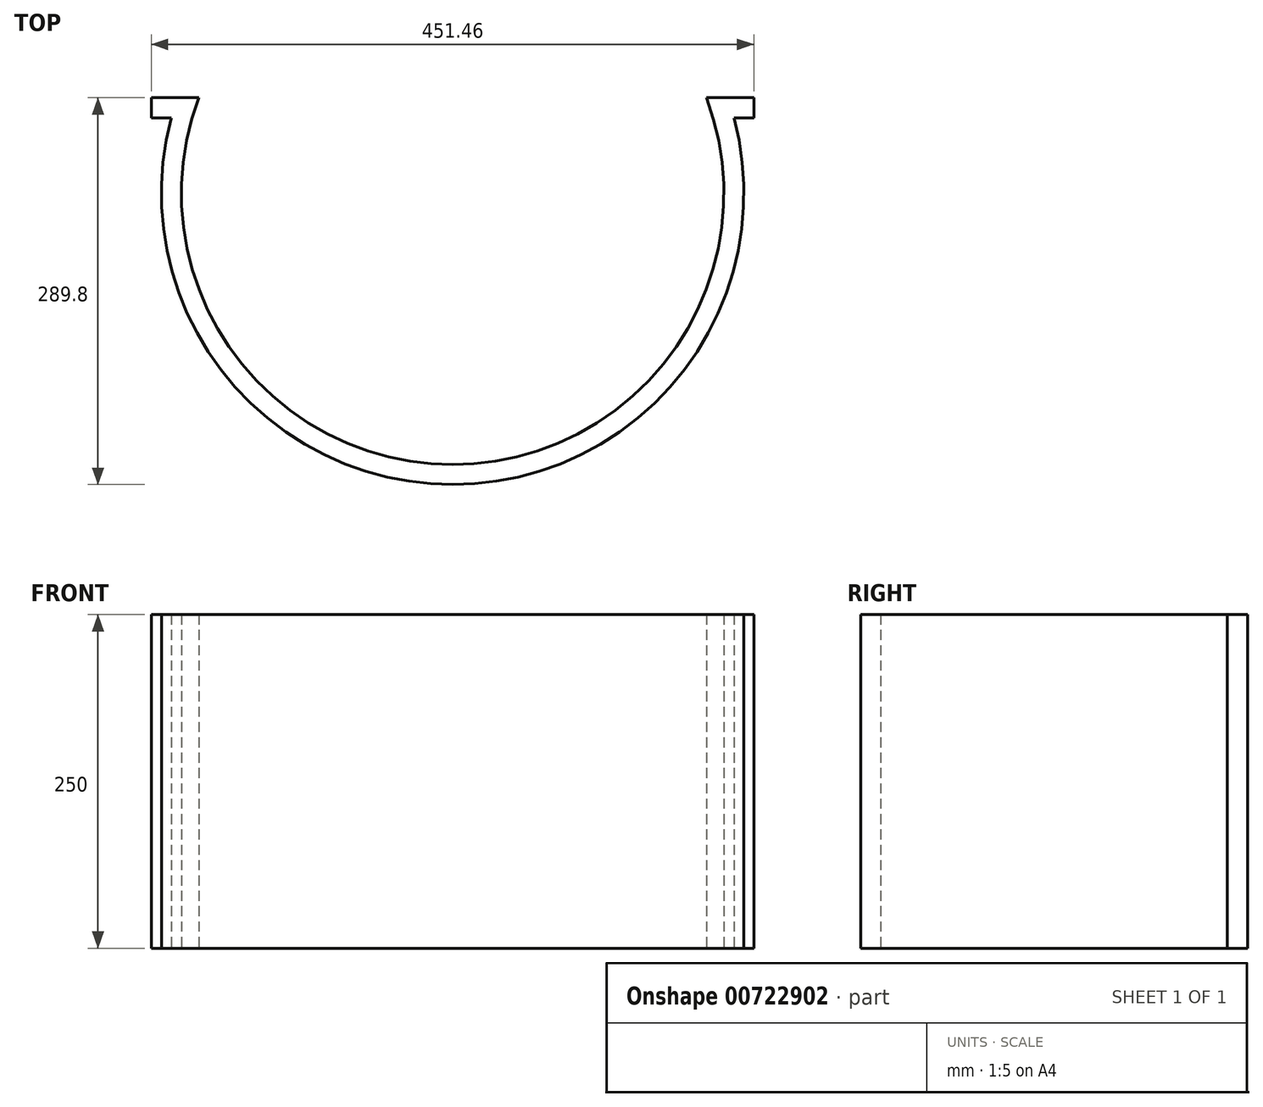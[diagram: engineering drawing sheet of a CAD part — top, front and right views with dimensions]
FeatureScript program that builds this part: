
annotation { "Feature Type Name" : "Feature", "Feature Type Description" : "" }
export const myFeature = defineFeature(function(context is Context, id is Id, definition is map)
    precondition{}
    {
        {
            var Q0;
            Q0=qCreatedBy(makeId("Top.planeOp"),FACE);
            var sketch = newSketch(context, id + "F0", { "sketchPlane" : qUnion([Q0])});
            skCircle(sketch, "E0", {"center": v(0, 0) * mm, "radius": 218.2 * mm});
            skCircle(sketch, "E1.0", {"center": v(0, 0) * mm, "radius": 203.2 * mm});
            skLineSegment(sketch, "E2", {"start": v(-206.12, 71.6) * mm, "end": v(206.12, 71.6) * mm});
            skLineSegment(sketch, "E3", {"start": v(206.12, 71.6) * mm, "end": v(225.73, 71.6) * mm});
            skLineSegment(sketch, "E4", {"start": v(225.73, 71.6) * mm, "end": v(225.73, 56.6) * mm});
            skLineSegment(sketch, "E5", {"start": v(225.73, 56.6) * mm, "end": v(210.73, 56.6) * mm});
            skLineSegment(sketch, "E6", {"start": v(-206.12, 71.6) * mm, "end": v(-225.73, 71.6) * mm});
            skLineSegment(sketch, "E7", {"start": v(-225.73, 71.6) * mm, "end": v(-225.73, 56.6) * mm});
            skLineSegment(sketch, "E8", {"start": v(-225.73, 56.6) * mm, "end": v(-210.73, 56.6) * mm});
            skSolve(sketch);
        }
        {
            var Q0;
            Q0=makeQuery(id+"F0.imprint","IMPRINT",FACE,{"disambiguationData":[TD([[makeQuery(id+"F0.imprint","IMPRINT",EDGE,{"derivedFrom":sQuery(id+"F0.wireOp",EDGE,"ID2K4z5C-0TQm-h0nz-zv6P-kyq5hynE2C9N")}),-1.0]])]});
            var Q1;
            {var subQ0=sQuery(id+"F0.wireOp",EDGE,"E1.0");var subQ1=sQuery(id+"F0.wireOp",EDGE,"3612953e-2b15-42a2-b21d-2527df8e02fb.0");var subQ2=makeQuery(id+"F0.imprint","INTERSECT",VERTEX,{"derivedFrom":[subQ1,subQ0]});Q1=makeQuery(id+"F0.imprint","IMPRINT",FACE,{"disambiguationData":[TD([[makeQuery(id+"F0.imprint","IMPRINT",EDGE,{"disambiguationData":[TD([[subQ2,-1.0]])],"derivedFrom":subQ1}),-1.0]])]});}
            var Q2;
            {var subQ0=sQuery(id+"F0.wireOp",EDGE,"E6");Q2=makeQuery(id+"F0.imprint","IMPRINT",FACE,{"disambiguationData":[TD([[makeQuery(id+"F0.imprint","IMPRINT",EDGE,{"derivedFrom":subQ0}),1.0]])]});}
            var Q3;
            {var subQ0=sQuery(id+"F0.wireOp",EDGE,"E1.0");var subQ1=sQuery(id+"F0.wireOp",EDGE,"3612953e-2b15-42a2-b21d-2527df8e02fb.2");var subQ2=makeQuery(id+"F0.imprint","INTERSECT",VERTEX,{"derivedFrom":[subQ1,subQ0]});Q3=makeQuery(id+"F0.imprint","IMPRINT",FACE,{"disambiguationData":[TD([[makeQuery(id+"F0.imprint","IMPRINT",EDGE,{"disambiguationData":[TD([[subQ2,-1.0]])],"derivedFrom":subQ1}),1.0]])]});}
            var Q4;
            {var subQ0=sQuery(id+"F0.wireOp",EDGE,"E3");Q4=makeQuery(id+"F0.imprint","IMPRINT",FACE,{"disambiguationData":[TD([[makeQuery(id+"F0.imprint","IMPRINT",EDGE,{"derivedFrom":subQ0}),-1.0]])]});}
            var Q5;
            {var subQ4=sQuery(id+"F0.wireOp",EDGE,"3612953e-2b15-42a2-b21d-2527df8e02fb.1");Q5=makeQuery(id+"F0.imprint","IMPRINT",FACE,{"disambiguationData":[TD([[makeQuery(id+"F0.imprint","IMPRINT",EDGE,{"derivedFrom":subQ4}),1.0]])]});}
            var Q6;
            {var subQ0=sQuery(id+"F0.wireOp",EDGE,"E0");var subQ1=makeQuery(id+"F0.imprint","INTERSECT",VERTEX,{"derivedFrom":[subQ0,sQuery(id+"F0.wireOp",EDGE,"E5")]});Q6=makeQuery(id+"F0.imprint","IMPRINT",FACE,{"disambiguationData":[TD([[makeQuery(id+"F0.imprint","IMPRINT",EDGE,{"disambiguationData":[TD([[subQ1,1.0]])],"derivedFrom":subQ0}),1.0]])]});}
            extrude(context, id + "F1", {"entities" : qUnion([Q0, Q1, Q2, Q3, Q4, Q5, Q6]), "depth" : 250 * mm, "offsetDistance" : 25 * mm});
        }
    });
